FCSTD DOCUMENT  (FreeCAD 0.20R29410 (Git))
Label: 60_Keyboard
License: All rights reserved
LicenseURL: http://en.wikipedia.org/wiki/All_rights_reserved
objects: Sketcher::SketchObject×4
note: 4 computed .brp shape members not serialized (recipe doc carries the construction recipe); baked Part::Feature solids carry a one-line shape summary decoded from their .brp

FEATURE [Sketcher::SketchObject] Sketch  label="TopProfile"
  FullyConstrained = true
  expr: Constraints[15] = .Constraints.WallThickness
  sketch-geometry (6):
    g0: LineSegment StartX=-145 StartY=51 StartZ=0 EndX=0 EndY=51 EndZ=0
    g1: LineSegment StartX=-147 StartY=49 StartZ=0 EndX=-145 EndY=51 EndZ=0
    g2: LineSegment StartX=-147 StartY=49 StartZ=0 EndX=-147 EndY=0 EndZ=0
    g3: LineSegment StartX=-143 StartY=0 StartZ=0 EndX=-143 EndY=44 EndZ=0
    g4: LineSegment StartX=0 StartY=47 StartZ=0 EndX=-140 EndY=47 EndZ=0
    g5: ArcOfCircle CenterX=-140 CenterY=44 CenterZ=0 NormalX=0 NormalY=0 NormalZ=1 AngleXU=0 Radius=3 StartAngle=1.5708 EndAngle=3.14159
  constraints (21):
    c: Horizontal(g0)
    c: DistanceX(g1,g0) = 147  'WallHalfWidth'
    c: Coincident(g1,g0)
    c: Coincident(g1,g2)
    c: PointOnObject(g2,g-1)
    c: Vertical(g2)
    c: Angle(g2,g1) = 2.35619
    c: DistanceY(g1,g0) = 2  'WallOuterChamfer'
    c: DistanceY(g-1,g0) = 51  'WallHalfDepth'
    c: PointOnObject(g0,g-2)
    c: PointOnObject(g3,g-1)
    c: Vertical(g3)
    c: PointOnObject(g4,g-2)
    c: Horizontal(g4)
    c: DistanceX(g2,g3) = 4  'WallThickness'
    c: DistanceY(g4,g0) = 4
    c: Coincident(g5,g3)
    c: Coincident(g5,g4)
    c: Vertical(g5,g4)
    c: Horizontal(g3,g5)
    c: Diameter(g5) = 6  'WallInnerFillet'
FEATURE [Sketcher::SketchObject] Sketch001  label="FrontProfile"
  ExternalGeometry = -> [Sketch]
  FullyConstrained = true
  Placement = pos=(0,0,0) rot=(1,0,0;1.5708rad)
  sketch-geometry (3):
    g0: LineSegment StartX=-147 StartY=0 StartZ=0 EndX=-147 EndY=-18 EndZ=0
    g1: LineSegment StartX=-147 StartY=0 StartZ=0 EndX=0 EndY=0 EndZ=0
    g2: LineSegment StartX=-147 StartY=-18 StartZ=0 EndX=0 EndY=-18 EndZ=0
  constraints (8):
    c: Coincident(g0,g-3)
    c: Vertical(g0)
    c: Coincident(g1,g0)
    c: Coincident(g1,g-1)
    c: DistanceY(g0,g0) = 18
    c: Coincident(g2,g0)
    c: PointOnObject(g2,g-2)
    c: Horizontal(g2)
FEATURE [Sketcher::SketchObject] Sketch002  label="RearProfile"
  ExternalGeometry = -> [Sketch]
  FullyConstrained = true
  Placement = pos=(0,0,0) rot=(0,0.707107,0.707107;3.14159rad)
  sketch-geometry (4):
    g0: LineSegment StartX=0 StartY=0 StartZ=0 EndX=147 EndY=0 EndZ=0
    g1: LineSegment StartX=147 StartY=0 StartZ=0 EndX=147 EndY=-22 EndZ=0
    g2: LineSegment StartX=147 StartY=-22 StartZ=0 EndX=135 EndY=-34 EndZ=0
    g3: LineSegment StartX=135 StartY=-34 StartZ=0 EndX=0 EndY=-34 EndZ=0
  constraints (11):
    c: Coincident(g-1,g0)
    c: Coincident(g0,g-3)
    c: Coincident(g0,g1)
    c: Vertical(g1)
    c: Coincident(g1,g2)
    c: Coincident(g2,g3)
    c: PointOnObject(g3,g-2)
    c: Horizontal(g3)
    c: DistanceY(g3,g0) = 34  'RearWallHeight'
    c: Angle(g2,g3) = 2.35619  'RearWallChamfer'
    c: DistanceY(g1,g1) = 22  'RearWallShortHeight'
FEATURE [Sketcher::SketchObject] Sketch003
  ExternalGeometry = -> [Sketch,Sketch001,Sketch002]
  FullyConstrained = true
  Placement = pos=(0,0,0) rot=(0.57735,0.57735,0.57735;2.0944rad)
